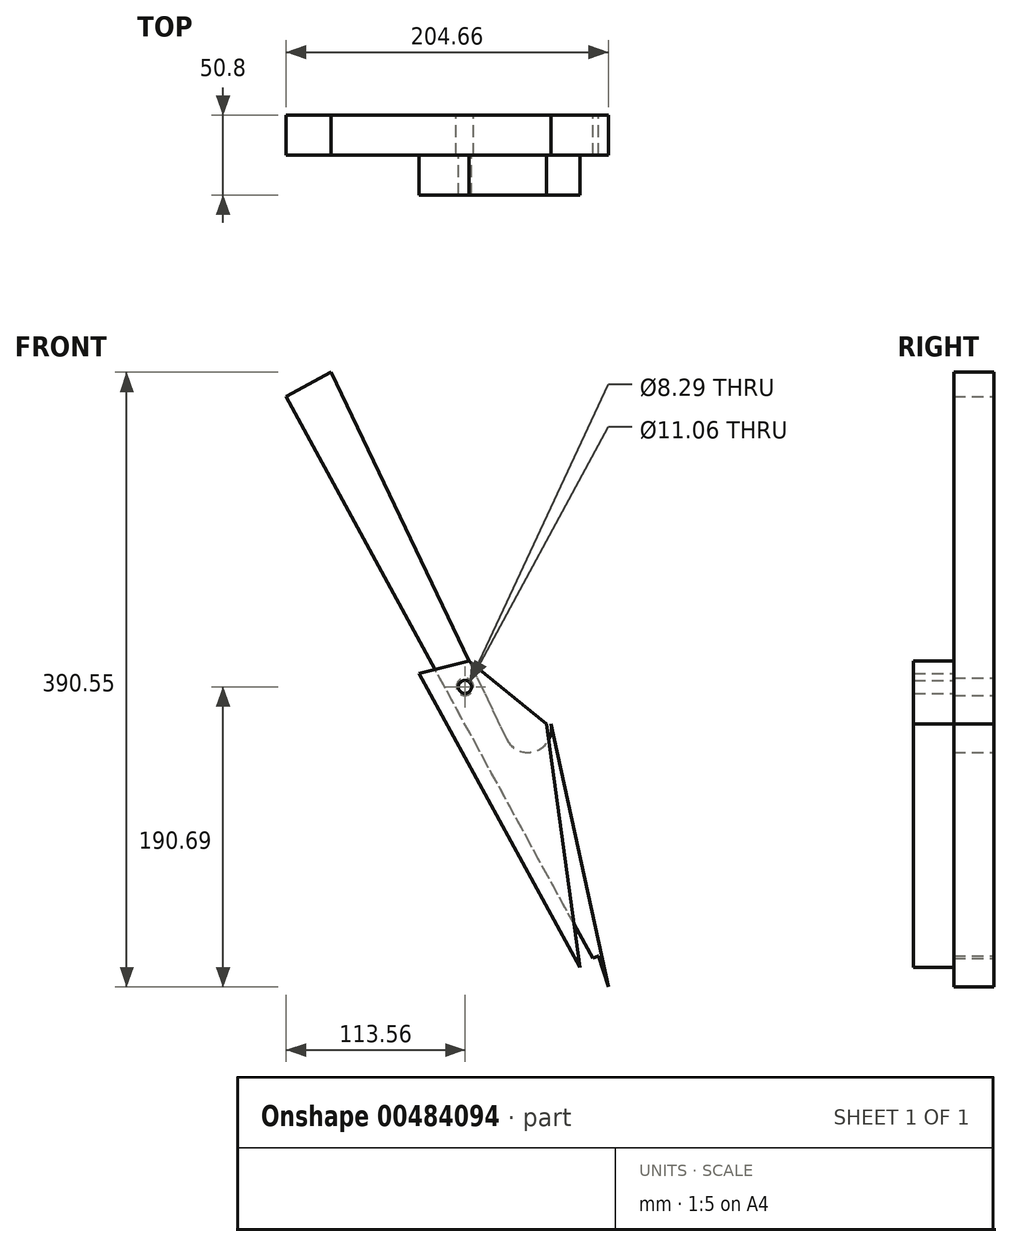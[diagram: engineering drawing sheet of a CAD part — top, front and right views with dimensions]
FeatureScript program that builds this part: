
annotation { "Feature Type Name" : "Feature", "Feature Type Description" : "" }
export const myFeature = defineFeature(function(context is Context, id is Id, definition is map)
    precondition{}
    {
        {
            var Q0;
            Q0=qCreatedBy(makeId("Front.planeOp"),FACE);
            var sketch = newSketch(context, id + "F0", { "sketchPlane" : qUnion([Q0])});
            skLineSegment(sketch, "E0", {"start": v(0, 0) * mm, "end": v(-51.14, 164.05) * mm});
            skCircle(sketch, "E1", {"center": v(-51.14, 164.05) * mm, "radius": 15 * mm});
            skCircle(sketch, "E2", {"center": v(-91.1, 190.7) * mm, "radius": 190.7 * mm});
            skLineSegment(sketch, "E3", {"start": v(-91.1, 190.7) * mm, "end": v(-38.4, 7.43) * mm});
            skLineSegment(sketch, "E4", {"start": v(0, 0) * mm, "end": v(-315.43, 0) * mm, "construction": true});
            skLineSegment(sketch, "E5", {"start": v(0, 0) * mm, "end": v(-36.49, 167.25) * mm});
            skLineSegment(sketch, "E6", {"start": v(0, 0) * mm, "end": v(-204.66, 375.06) * mm});
            skLineSegment(sketch, "E7", {"start": v(-204.66, 375.06) * mm, "end": v(-176.28, 390.55) * mm});
            skLineSegment(sketch, "E8", {"start": v(-176.28, 390.55) * mm, "end": v(-64.67, 157.57) * mm});
            skCircle(sketch, "E9", {"center": v(-91.1, 190.7) * mm, "radius": 5.53 * mm});
            skSolve(sketch);
        }
        {
            var Q0;
            {var subQ7=sQuery(id+"F0.wireOp",EDGE,"E0");var subQ9=sQuery(id+"F0.wireOp",EDGE,"E1");var subQ11=makeQuery(id+"F0.imprint","INTERSECT",VERTEX,{"derivedFrom":[subQ7,subQ9]});Q0=makeQuery(id+"F0.imprint","IMPRINT",FACE,{"disambiguationData":[TD([[makeQuery(id+"F0.imprint","IMPRINT",EDGE,{"disambiguationData":[TD([[subQ11,1.0]])],"derivedFrom":subQ7}),1.0]])]});}
            var Q1;
            {var subQ0=sQuery(id+"F0.wireOp",EDGE,"E1");var subQ1=sQuery(id+"F0.wireOp",EDGE,"E0");var subQ2=makeQuery(id+"F0.imprint","INTERSECT",VERTEX,{"derivedFrom":[subQ1,subQ0]});Q1=makeQuery(id+"F0.imprint","IMPRINT",FACE,{"disambiguationData":[TD([[makeQuery(id+"F0.imprint","IMPRINT",EDGE,{"disambiguationData":[TD([[subQ2,1.0]])],"derivedFrom":subQ1}),-1.0]])]});}
            var Q2;
            {var subQ5=sQuery(id+"F0.wireOp",EDGE,"E7");Q2=makeQuery(id+"F0.imprint","IMPRINT",FACE,{"disambiguationData":[TD([[makeQuery(id+"F0.imprint","IMPRINT",EDGE,{"derivedFrom":subQ5}),-1.0]])]});}
            var Q3;
            {var subQ0=sQuery(id+"F0.wireOp",EDGE,"E6");var subQ3=sQuery(id+"F0.wireOp",EDGE,"E2");var subQ5=makeQuery(id+"F0.imprint","INTERSECT",VERTEX,{"disambiguationData":[OD(1.0)],"derivedFrom":[subQ3,subQ0]});Q3=makeQuery(id+"F0.imprint","IMPRINT",FACE,{"disambiguationData":[TD([[makeQuery(id+"F0.imprint","IMPRINT",EDGE,{"disambiguationData":[TD([[subQ5,-1.0]])],"derivedFrom":subQ3}),-1.0]])]});}
            var Q4;
            {var subQ0=sQuery(id+"F0.wireOp",EDGE,"E5");var subQ3=sQuery(id+"F0.wireOp",EDGE,"E2");var subQ5=makeQuery(id+"F0.imprint","INTERSECT",VERTEX,{"derivedFrom":[subQ3,subQ0]});Q4=makeQuery(id+"F0.imprint","IMPRINT",FACE,{"disambiguationData":[TD([[makeQuery(id+"F0.imprint","IMPRINT",EDGE,{"disambiguationData":[TD([[subQ5,1.0]])],"derivedFrom":subQ3}),-1.0]])]});}
            extrude(context, id + "F1", {"entities" : qUnion([Q0, Q1, Q2, Q3, Q4]), "depth" : 25.4 * mm});
        }
        {
            var Q0;
            Q0=makeQuery(id+"F1.opExtrude","CAP_FACE",FACE,{"disambiguationData":[OSD([sQuery(id+"F0.wireOp",EDGE,"E1"),sQuery(id+"F0.wireOp",EDGE,"E5"),sQuery(id+"F0.wireOp",EDGE,"E6"),sQuery(id+"F0.wireOp",EDGE,"E7"),sQuery(id+"F0.wireOp",EDGE,"E8"),sQuery(id+"F0.wireOp",EDGE,"E9")])],"isStart":false});
            var sketch = newSketch(context, id + "F2", { "sketchPlane" : qUnion([Q0])});
            skCircle(sketch, "E10", {"center": v(-91.1, 190.7) * mm, "radius": 4.14 * mm});
            skLineSegment(sketch, "E11", {"start": v(-91.1, 190.7) * mm, "end": v(-117.14, 0) * mm, "construction": true});
            skCircle(sketch, "E12", {"center": v(-91.1, 190.7) * mm, "radius": 192.46 * mm, "construction": true});
            skLineSegment(sketch, "E13", {"start": v(-91.1, 190.7) * mm, "end": v(-18.13, 12.6) * mm, "construction": true});
            skLineSegment(sketch, "E14", {"start": v(-18.13, 12.6) * mm, "end": v(-120.3, 199.13) * mm});
            skLineSegment(sketch, "E15", {"start": v(-120.3, 199.13) * mm, "end": v(-88.42, 207.15) * mm});
            skLineSegment(sketch, "E16", {"start": v(-88.42, 207.15) * mm, "end": v(-39.33, 167.23) * mm});
            skLineSegment(sketch, "E17", {"start": v(-39.33, 167.23) * mm, "end": v(-18.13, 12.6) * mm});
            skSolve(sketch);
        }
        {
            var Q0;
            Q0 = qSketchRegion(id + "F2", true);
            extrude(context, id + "F3", {"entities" : qUnion([Q0]), "depth" : 25.4 * mm});
        }
    });
